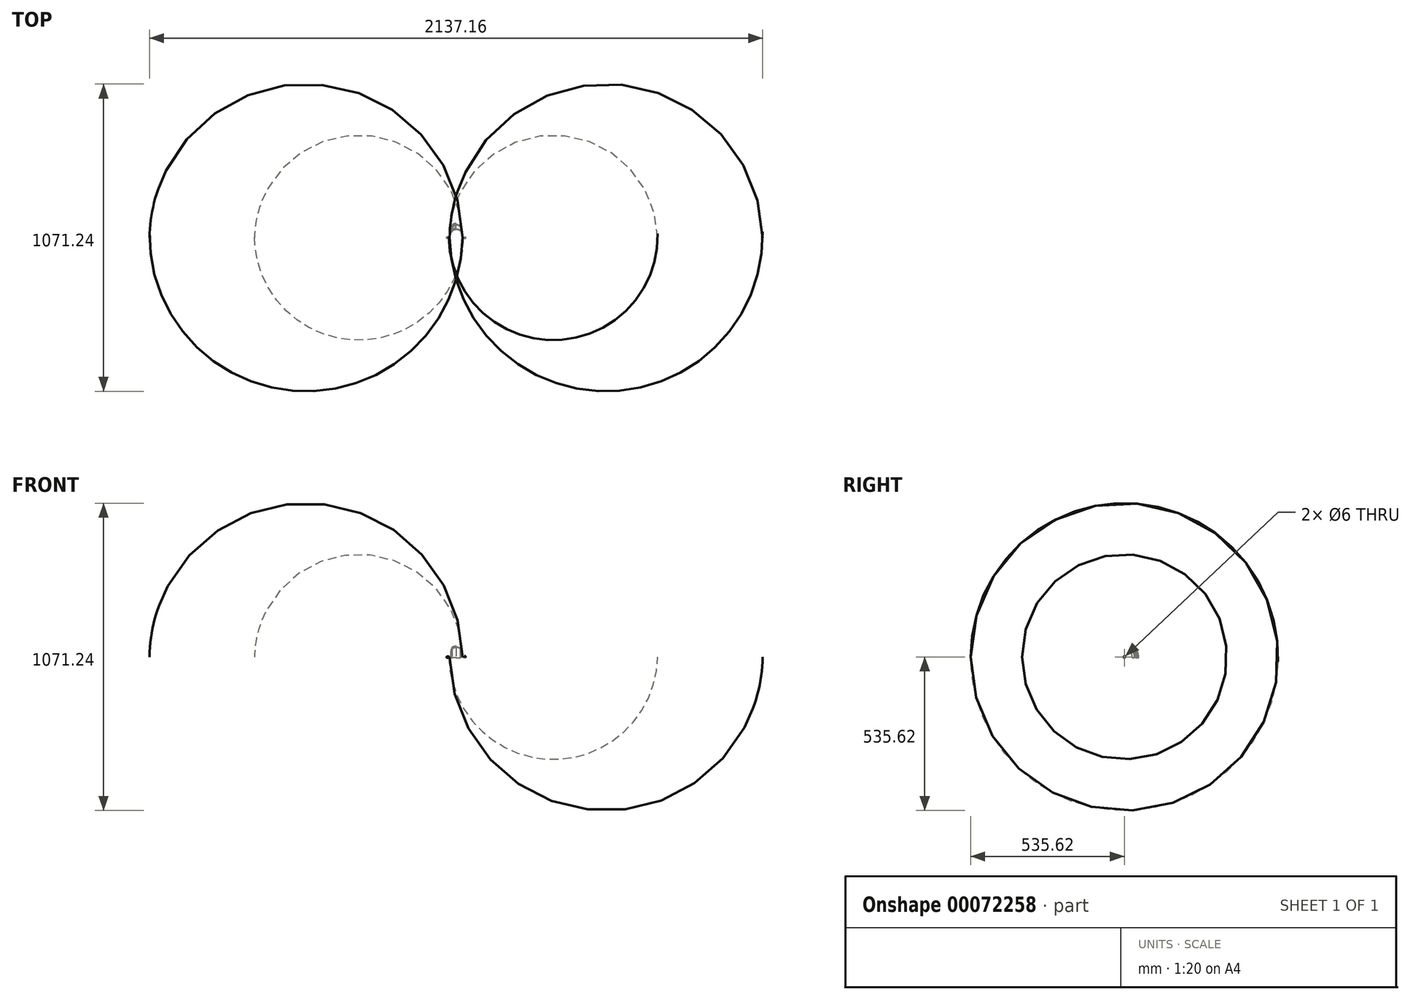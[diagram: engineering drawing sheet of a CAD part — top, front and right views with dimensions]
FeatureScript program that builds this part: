
annotation { "Feature Type Name" : "Feature", "Feature Type Description" : "" }
export const myFeature = defineFeature(function(context is Context, id is Id, definition is map)
    precondition{}
    {
        {
            var Q0;
            Q0=qCreatedBy(makeId("Top.planeOp"),FACE);
            var sketch = newSketch(context, id + "F0", { "sketchPlane" : qUnion([Q0])});
            skLineSegment(sketch, "E0", {"start": v(-20, 0) * mm, "end": v(20, 0) * mm, "construction": true});
            skLineSegment(sketch, "E1", {"start": v(-20, 0) * mm, "end": v(-20, 80) * mm, "construction": true});
            skLineSegment(sketch, "E2", {"start": v(20, 0) * mm, "end": v(20, 80) * mm, "construction": true});
            skFitSpline(sketch, "E3", {"points": [v(-20, 0) * mm, v(20, 0) * mm], "startDerivative": vector(0, 240) * mm, "endDerivative": vector(0, -240) * mm});
            skLineSegment(sketch, "E4", {"start": v(-20, 0) * mm, "end": v(-20, -3) * mm});
            skLineSegment(sketch, "E5", {"start": v(20, 0) * mm, "end": v(20, -3) * mm});
            skLineSegment(sketch, "E6", {"start": v(-23.64, 0.35) * mm, "end": v(-22.57, 1.42) * mm});
            skLineSegment(sketch, "E7", {"start": v(-23.64, -0.35) * mm, "end": v(-22, -2) * mm});
            skLineSegment(sketch, "E8", {"start": v(-22, -2) * mm, "end": v(-22, -3) * mm});
            skFitSpline(sketch, "E9.0", {"points": [v(-22, 0) * mm, v(-22, 6.8) * mm, v(-21.05, 15.75) * mm, v(-18.3, 25.26) * mm, v(-15.59, 31.18) * mm, v(-12.32, 35.89) * mm, v(-8.57, 39.35) * mm, v(-4.42, 41.5) * mm, v(0, 42.25) * mm, v(4.42, 41.5) * mm, v(8.57, 39.35) * mm, v(12.32, 35.89) * mm, v(15.59, 31.18) * mm, v(18.3, 25.26) * mm, v(21.05, 15.75) * mm, v(22, 6.8) * mm, v(22, 0) * mm]});
            skLineSegment(sketch, "E10", {"start": v(-22, -3) * mm, "end": v(-20, -3) * mm});
            skFitSpline(sketch, "E11.0", {"points": [v(-22.5, 0) * mm, v(-22.5, 6.82) * mm, v(-21.54, 15.84) * mm, v(-18.77, 25.43) * mm, v(-16.03, 31.43) * mm, v(-12.7, 36.21) * mm, v(-8.87, 39.76) * mm, v(-4.58, 41.99) * mm, v(0, 42.76) * mm, v(4.58, 41.99) * mm, v(8.87, 39.76) * mm, v(12.7, 36.21) * mm, v(16.03, 31.43) * mm, v(18.77, 25.43) * mm, v(21.54, 15.84) * mm, v(22.5, 6.82) * mm, v(22.5, 0) * mm]});
            skLineSegment(sketch, "E12", {"start": v(-23.57, 1.42) * mm, "end": v(-24.64, 0.35) * mm});
            skLineSegment(sketch, "E13", {"start": v(-24.64, -0.35) * mm, "end": v(-23, -2) * mm});
            skLineSegment(sketch, "E14", {"start": v(-23, -2) * mm, "end": v(-23, -3) * mm});
            skLineSegment(sketch, "E15", {"start": v(-23, -3) * mm, "end": v(-24.98, -3) * mm});
            skLineSegment(sketch, "E16", {"start": v(-24.98, -3) * mm, "end": v(-24.98, -2) * mm});
            skLineSegment(sketch, "E17", {"start": v(-24.98, -2) * mm, "end": v(-26.63, -0.35) * mm});
            skLineSegment(sketch, "E18", {"start": v(-26.63, 0.35) * mm, "end": v(-25.57, 1.41) * mm});
            skFitSpline(sketch, "E19.0", {"points": [v(-24.5, 0) * mm, v(-24.5, 6.95) * mm, v(-23.53, 16.17) * mm, v(-20.65, 26.12) * mm, v(-17.78, 32.4) * mm, v(-14.24, 37.51) * mm, v(-10.75, 40.75) * mm, v(-7.65, 42.65) * mm, v(-5.2, 43.7) * mm, v(-2.62, 44.35) * mm, v(0, 44.57) * mm, v(2.62, 44.35) * mm, v(5.2, 43.7) * mm, v(7.65, 42.65) * mm, v(10.75, 40.75) * mm, v(14.24, 37.51) * mm, v(17.78, 32.4) * mm, v(20.65, 26.12) * mm, v(23.53, 16.17) * mm, v(24.5, 6.95) * mm, v(24.5, 0) * mm]});
            skLineSegment(sketch, "E20", {"start": v(0, 0) * mm, "end": v(0, 79.47) * mm});
            skPoint(sketch, "E21", {"position": v(0, 60) * mm});
            skFitSpline(sketch, "E22.0", {"points": [v(-25, 0) * mm, v(-25, 6.98) * mm, v(-24.02, 16.26) * mm, v(-21.13, 26.29) * mm, v(-18.22, 32.65) * mm, v(-14.63, 37.84) * mm, v(-11.06, 41.14) * mm, v(-7.88, 43.1) * mm, v(-5.35, 44.18) * mm, v(-2.7, 44.85) * mm, v(0, 45.08) * mm, v(2.7, 44.85) * mm, v(5.35, 44.18) * mm, v(7.88, 43.1) * mm, v(11.06, 41.14) * mm, v(14.63, 37.84) * mm, v(18.22, 32.65) * mm, v(21.13, 26.29) * mm, v(24.02, 16.26) * mm, v(25, 6.98) * mm, v(25, 0) * mm]});
            skLineSegment(sketch, "E23", {"start": v(-25.98, -3) * mm, "end": v(-25.98, -2) * mm});
            skLineSegment(sketch, "E24", {"start": v(-25.98, -2) * mm, "end": v(-27.63, -0.35) * mm});
            skLineSegment(sketch, "E25", {"start": v(-27.63, 0.35) * mm, "end": v(-26.57, 1.41) * mm});
            skFitSpline(sketch, "E26.0", {"points": [v(-27, 0) * mm, v(-27, 7.1) * mm, v(-26, 16.6) * mm, v(-23.01, 26.97) * mm, v(-19.98, 33.62) * mm, v(-16.17, 39.14) * mm, v(-12.3, 42.73) * mm, v(-8.81, 44.88) * mm, v(-6, 46.08) * mm, v(-3.04, 46.83) * mm, v(0, 47.09) * mm, v(3.04, 46.83) * mm, v(6, 46.08) * mm, v(8.81, 44.88) * mm, v(12.3, 42.73) * mm, v(16.17, 39.14) * mm, v(19.98, 33.62) * mm, v(23.01, 26.97) * mm, v(26, 16.6) * mm, v(27, 7.1) * mm, v(27, 0) * mm]});
            skLineSegment(sketch, "E27", {"start": v(-27.97, -3) * mm, "end": v(-27.97, -2) * mm});
            skLineSegment(sketch, "E28", {"start": v(-27.97, -2) * mm, "end": v(-29.62, -0.35) * mm});
            skLineSegment(sketch, "E29", {"start": v(-27.97, -3) * mm, "end": v(-25.98, -3) * mm});
            skLineSegment(sketch, "E30", {"start": v(-29.62, 0.35) * mm, "end": v(-28.57, 1.4) * mm});
            skLineSegment(sketch, "E31", {"start": v(0, 3) * mm, "end": v(-44.65, 3) * mm});
            skLineSegment(sketch, "E32", {"start": v(-20, 0) * mm, "end": v(-44.65, 0) * mm});
            skFitSpline(sketch, "E33.0", {"points": [v(-27.5, 0) * mm, v(-27.5, 7.13) * mm, v(-26.5, 16.68) * mm, v(-23.49, 27.14) * mm, v(-20.42, 33.86) * mm, v(-16.55, 39.46) * mm, v(-12.62, 43.12) * mm, v(-9.04, 45.32) * mm, v(-6.16, 46.56) * mm, v(-3.12, 47.32) * mm, v(0, 47.59) * mm, v(3.12, 47.32) * mm, v(6.16, 46.56) * mm, v(9.04, 45.32) * mm, v(12.62, 43.12) * mm, v(16.55, 39.46) * mm, v(20.42, 33.86) * mm, v(23.49, 27.14) * mm, v(26.5, 16.68) * mm, v(27.5, 7.13) * mm, v(27.5, 0) * mm]});
            skFitSpline(sketch, "E34.0", {"points": [v(-29.5, 0) * mm, v(-29.5, 7.26) * mm, v(-28.49, 17.01) * mm, v(-25.37, 27.82) * mm, v(-22.18, 34.84) * mm, v(-18.1, 40.77) * mm, v(-13.87, 44.7) * mm, v(-9.97, 47.1) * mm, v(-6.8, 48.46) * mm, v(-3.46, 49.3) * mm, v(0, 49.6) * mm, v(3.46, 49.3) * mm, v(6.8, 48.46) * mm, v(9.97, 47.1) * mm, v(13.87, 44.7) * mm, v(18.1, 40.77) * mm, v(22.18, 34.84) * mm, v(25.37, 27.82) * mm, v(28.49, 17.01) * mm, v(29.5, 7.26) * mm, v(29.5, 0) * mm]});
            skLineSegment(sketch, "E35", {"start": v(-28.97, -3) * mm, "end": v(-30.97, -3) * mm});
            skLineSegment(sketch, "E36", {"start": v(-30.97, -3) * mm, "end": v(-30.97, -2) * mm});
            skLineSegment(sketch, "E37", {"start": v(-30.97, -2) * mm, "end": v(-32.97, 0) * mm});
            skLineSegment(sketch, "E38", {"start": v(-28.97, -3) * mm, "end": v(-28.97, -2) * mm});
            skLineSegment(sketch, "E39", {"start": v(-28.97, -2) * mm, "end": v(-30.62, -0.35) * mm});
            skLineSegment(sketch, "E40", {"start": v(-30.62, 0.35) * mm, "end": v(-29.57, 1.4) * mm});
            skPoint(sketch, "E41.visualSharp", {"position": v(-30.97, 0) * mm});
            skArc(sketch, "E41.filletArc", {"start": v(-30.62, 0.35) * mm, "mid": v(-30.77, 0) * mm, "end": v(-30.62, -0.35) * mm});
            skPoint(sketch, "E42.visualSharp", {"position": v(-29.97, 0) * mm});
            skArc(sketch, "E42.filletArc", {"start": v(-29.62, 0.35) * mm, "mid": v(-29.77, 0) * mm, "end": v(-29.62, -0.35) * mm});
            skPoint(sketch, "E43.visualSharp", {"position": v(-27.98, 0) * mm});
            skArc(sketch, "E43.filletArc", {"start": v(-27.63, 0.35) * mm, "mid": v(-27.78, 0) * mm, "end": v(-27.63, -0.35) * mm});
            skPoint(sketch, "E44.visualSharp", {"position": v(-26.98, 0) * mm});
            skArc(sketch, "E44.filletArc", {"start": v(-26.63, 0.35) * mm, "mid": v(-26.78, 0) * mm, "end": v(-26.63, -0.35) * mm});
            skPoint(sketch, "E45.visualSharp", {"position": v(-25, 0) * mm});
            skArc(sketch, "E45.filletArc", {"start": v(-24.64, 0.35) * mm, "mid": v(-24.78, 0) * mm, "end": v(-24.64, -0.35) * mm});
            skPoint(sketch, "E46.visualSharp", {"position": v(-24, 0) * mm});
            skArc(sketch, "E46.filletArc", {"start": v(-23.64, 0.35) * mm, "mid": v(-23.78, 0) * mm, "end": v(-23.64, -0.35) * mm});
            skPoint(sketch, "E47.visualSharp", {"position": v(-29, 1.98) * mm});
            skArc(sketch, "E47.filletArc", {"start": v(-29.57, 1.4) * mm, "mid": v(-29.14, 2.04) * mm, "end": v(-28.98, 2.8) * mm});
            skPoint(sketch, "E48.visualSharp", {"position": v(-28, 1.98) * mm});
            skArc(sketch, "E48.filletArc", {"start": v(-28.57, 1.4) * mm, "mid": v(-28.14, 2.04) * mm, "end": v(-27.98, 2.8) * mm});
            skPoint(sketch, "E49.visualSharp", {"position": v(-26, 2) * mm});
            skArc(sketch, "E49.filletArc", {"start": v(-26.57, 1.41) * mm, "mid": v(-26.14, 2.05) * mm, "end": v(-25.98, 2.8) * mm});
            skPoint(sketch, "E50.visualSharp", {"position": v(-25, 2) * mm});
            skArc(sketch, "E50.filletArc", {"start": v(-25.57, 1.41) * mm, "mid": v(-25.14, 2.05) * mm, "end": v(-24.98, 2.8) * mm});
            skPoint(sketch, "E51.visualSharp", {"position": v(-23, 2) * mm});
            skArc(sketch, "E51.filletArc", {"start": v(-23.57, 1.42) * mm, "mid": v(-23.14, 2.06) * mm, "end": v(-22.98, 2.81) * mm});
            skPoint(sketch, "E52.visualSharp", {"position": v(-22, 2) * mm});
            skArc(sketch, "E52.filletArc", {"start": v(-22.57, 1.42) * mm, "mid": v(-22.14, 2.06) * mm, "end": v(-21.98, 2.81) * mm});
            skLineSegment(sketch, "E53", {"start": v(-32.77, 0) * mm, "end": v(-32.77, 1.17) * mm});
            skLineSegment(sketch, "E54", {"start": v(-32.18, 2.59) * mm, "end": v(-31.54, 3.23) * mm});
            skPoint(sketch, "E55.visualSharp", {"position": v(-32.77, 2) * mm});
            skArc(sketch, "E55.filletArc", {"start": v(-32.18, 2.59) * mm, "mid": v(-32.62, 1.94) * mm, "end": v(-32.77, 1.17) * mm});
            skPoint(sketch, "E56.visualSharp", {"position": v(-30.97, 3.8) * mm});
            skArc(sketch, "E56.filletArc", {"start": v(-31.54, 3.23) * mm, "mid": v(-31.12, 3.86) * mm, "end": v(-30.96, 4.6) * mm});
            skSolve(sketch);
        }
        {
            var Q0;
            {var subQ0=sQuery(id+"F0.wireOp",EDGE,"E26.0");var subQ3=sQuery(id+"F0.wireOp",EDGE,"E20");var subQ4=makeQuery(id+"F0.imprint","INTERSECT",VERTEX,{"derivedFrom":[subQ3,subQ0]});Q0=makeQuery(id+"F0.imprint","IMPRINT",FACE,{"disambiguationData":[TD([[makeQuery(id+"F0.imprint","IMPRINT",EDGE,{"disambiguationData":[TD([[subQ4,1.0]])],"derivedFrom":subQ3}),1.0]])]});}
            var Q1;
            {var subQ2=sQuery(id+"F0.wireOp",EDGE,"E25");Q1=makeQuery(id+"F0.imprint","IMPRINT",FACE,{"disambiguationData":[TD([[makeQuery(id+"F0.imprint","IMPRINT",EDGE,{"derivedFrom":subQ2}),1.0]])]});}
            var Q2;
            {var subQ3=sQuery(id+"F0.wireOp",EDGE,"E11.0");var subQ5=sQuery(id+"F0.wireOp",EDGE,"E20");var subQ7=makeQuery(id+"F0.imprint","INTERSECT",VERTEX,{"derivedFrom":[subQ3,subQ5]});Q2=makeQuery(id+"F0.imprint","IMPRINT",FACE,{"disambiguationData":[TD([[makeQuery(id+"F0.imprint","IMPRINT",EDGE,{"disambiguationData":[TD([[subQ7,1.0]])],"derivedFrom":subQ3}),1.0]])]});}
            var Q3;
            {var subQ2=sQuery(id+"F0.wireOp",EDGE,"E12");Q3=makeQuery(id+"F0.imprint","IMPRINT",FACE,{"disambiguationData":[TD([[makeQuery(id+"F0.imprint","IMPRINT",EDGE,{"derivedFrom":subQ2}),-1.0]])]});}
            var Q4;
            {var subQ3=sQuery(id+"F0.wireOp",EDGE,"E3");var subQ5=sQuery(id+"F0.wireOp",EDGE,"E20");var subQ7=makeQuery(id+"F0.imprint","INTERSECT",VERTEX,{"derivedFrom":[subQ3,subQ5]});Q4=makeQuery(id+"F0.imprint","IMPRINT",FACE,{"disambiguationData":[TD([[makeQuery(id+"F0.imprint","IMPRINT",EDGE,{"disambiguationData":[TD([[subQ7,1.0]])],"derivedFrom":subQ3}),1.0]])]});}
            var Q5;
            {var subQ5=sQuery(id+"F0.wireOp",EDGE,"E6");Q5=makeQuery(id+"F0.imprint","IMPRINT",FACE,{"disambiguationData":[TD([[makeQuery(id+"F0.imprint","IMPRINT",EDGE,{"derivedFrom":subQ5}),-1.0]])]});}
            var Q6;
            {var subQ3=sQuery(id+"F0.wireOp",EDGE,"E20");var subQ5=sQuery(id+"F0.wireOp",EDGE,"E34.0");var subQ7=makeQuery(id+"F0.imprint","INTERSECT",VERTEX,{"derivedFrom":[subQ3,subQ5]});Q6=makeQuery(id+"F0.imprint","IMPRINT",FACE,{"disambiguationData":[TD([[makeQuery(id+"F0.imprint","IMPRINT",EDGE,{"disambiguationData":[TD([[subQ7,1.0]])],"derivedFrom":subQ3}),1.0]])]});}
            var Q7;
            {var subQ1=sQuery(id+"F0.wireOp",EDGE,"f8a881d8-7a77-49e3-81df-cd23f309ca32");Q7=makeQuery(id+"F0.imprint","IMPRINT",FACE,{"disambiguationData":[TD([[makeQuery(id+"F0.imprint","IMPRINT",EDGE,{"derivedFrom":subQ1}),-1.0]])]});}
            var Q8;
            {var subQ5=sQuery(id+"F0.wireOp",EDGE,"E40");Q8=makeQuery(id+"F0.imprint","IMPRINT",FACE,{"disambiguationData":[TD([[makeQuery(id+"F0.imprint","IMPRINT",EDGE,{"derivedFrom":subQ5}),1.0]])]});}
            var Q9;
            Q9=sQuery(id+"F0.wireOp",EDGE,"E0");
            revolve(context, id + "F1", {"entities" : qUnion([Q0, Q1, Q2, Q3, Q4, Q5, Q6, Q7, Q8]), "axis" : qUnion([Q9]), "revolveType" : RevolveType.FULL});
        }
        {
            var Q0;
            Q0=qCreatedBy(makeId("Right.planeOp"),FACE);
            var sketch = newSketch(context, id + "F2", { "sketchPlane" : qUnion([Q0])});
            skCircle(sketch, "E57", {"center": v(0, 0) * mm, "radius": 3 * mm});
            skLineSegment(sketch, "E58", {"start": v(-2.12, 2.12) * mm, "end": v(69.28, 73.52) * mm});
            skLineSegment(sketch, "E59", {"start": v(0, -3) * mm, "end": v(100.98, -3) * mm});
            skArc(sketch, "E60", {"start": v(100.98, -3) * mm, "mid": v(93.33, 38.66) * mm, "end": v(69.28, 73.52) * mm});
            skSolve(sketch);
        }
        {
            var Q0;
            {var subQ1=sQuery(id+"F2.wireOp",EDGE,"E58");Q0=makeQuery(id+"F2.imprint","IMPRINT",FACE,{"disambiguationData":[TD([[makeQuery(id+"F2.imprint","IMPRINT",EDGE,{"derivedFrom":subQ1}),-1.0]])]});}
            var Q1;
            {var subQ0=sQuery(id+"F2.wireOp",EDGE,"E57");var subQ2=makeQuery(id+"F2.imprint","INTERSECT",VERTEX,{"derivedFrom":[subQ0,sQuery(id+"F2.wireOp",EDGE,"E58")]});Q1=makeQuery(id+"F2.imprint","IMPRINT",FACE,{"disambiguationData":[TD([[makeQuery(id+"F2.imprint","IMPRINT",EDGE,{"disambiguationData":[TD([[subQ2,-1.0]])],"derivedFrom":subQ0}),1.0]])]});}
            extrude(context, id + "F3", {"entities" : qUnion([Q0, Q1]), "operationType" : NewBodyOperationType.INTERSECT, "endBound" : BoundingType.THROUGH_ALL, "oppositeDirection" : true, "depth" : 102.9 * mm});
        }
        {
            var Q0;
            Q0=makeQuery(id+"F1.opRevolve","SWEPT_BODY",BODY,{"disambiguationData":[OSD([sQuery(id+"F0.wireOp",EDGE,"E3"),sQuery(id+"F0.wireOp",EDGE,"E6"),sQuery(id+"F0.wireOp",EDGE,"E9.0"),sQuery(id+"F0.wireOp",EDGE,"E20"),sQuery(id+"F0.wireOp",EDGE,"E32"),sQuery(id+"F0.wireOp",EDGE,"E46.filletArc"),sQuery(id+"F0.wireOp",EDGE,"E52.filletArc")])]});
            var Q1;
            Q1=makeQuery(id+"F1.opRevolve","SWEPT_BODY",BODY,{"disambiguationData":[OSD([sQuery(id+"F0.wireOp",EDGE,"E11.0"),sQuery(id+"F0.wireOp",EDGE,"E12"),sQuery(id+"F0.wireOp",EDGE,"E18"),sQuery(id+"F0.wireOp",EDGE,"E19.0"),sQuery(id+"F0.wireOp",EDGE,"E20"),sQuery(id+"F0.wireOp",EDGE,"E32"),sQuery(id+"F0.wireOp",EDGE,"E44.filletArc"),sQuery(id+"F0.wireOp",EDGE,"E45.filletArc"),sQuery(id+"F0.wireOp",EDGE,"E50.filletArc"),sQuery(id+"F0.wireOp",EDGE,"E51.filletArc")])]});
            var Q2;
            Q2=makeQuery(id+"F1.opRevolve","SWEPT_BODY",BODY,{"disambiguationData":[OSD([sQuery(id+"F0.wireOp",EDGE,"E20"),sQuery(id+"F0.wireOp",EDGE,"E22.0"),sQuery(id+"F0.wireOp",EDGE,"E25"),sQuery(id+"F0.wireOp",EDGE,"E26.0"),sQuery(id+"F0.wireOp",EDGE,"E30"),sQuery(id+"F0.wireOp",EDGE,"E32"),sQuery(id+"F0.wireOp",EDGE,"E42.filletArc"),sQuery(id+"F0.wireOp",EDGE,"E43.filletArc"),sQuery(id+"F0.wireOp",EDGE,"E48.filletArc"),sQuery(id+"F0.wireOp",EDGE,"E49.filletArc")])]});
            var Q3;
            Q3=makeQuery(id+"F1.opRevolve","SWEPT_BODY",BODY,{"disambiguationData":[OSD([sQuery(id+"F0.wireOp",EDGE,"E20"),sQuery(id+"F0.wireOp",EDGE,"E32"),sQuery(id+"F0.wireOp",EDGE,"E33.0"),sQuery(id+"F0.wireOp",EDGE,"E34.0"),sQuery(id+"F0.wireOp",EDGE,"E40"),sQuery(id+"F0.wireOp",EDGE,"E41.filletArc"),sQuery(id+"F0.wireOp",EDGE,"E47.filletArc"),sQuery(id+"F0.wireOp",EDGE,"E53"),sQuery(id+"F0.wireOp",EDGE,"E54")])]});
            var Q4;
            {var subQ0=sQuery(id+"F0.wireOp",EDGE,"E20");Q4=makeQuery(id+"F1.opRevolve","SWEPT_FACE",FACE,{"disambiguationData":[OSD([subQ0]),TDD([makeQuery(id+"F0.imprint","IMPRINT",EDGE,{"disambiguationData":[TD([[makeQuery(id+"F0.imprint","INTERSECT",VERTEX,{"derivedFrom":[subQ0,sQuery(id+"F0.wireOp",EDGE,"E34.0")]}),1.0]])],"derivedFrom":subQ0})])]});}
            mirror(context, id + "F4", {"operationType" : NewBodyOperationType.ADD, "entities" : qUnion([Q0, Q1, Q2, Q3]), "mirrorPlane" : qUnion([Q4])});
        }
    });
